# Revit family: Double_Check_Valve_Assembly-Backflow_Preventor-WATTS-LF909-909-AGK-NRS_Series.rfaxxx
name_source: partatom
category: Pipe Accessories
units: mm (PartAtom-declared; Revit-internal decimal feet)

## family parameters
Always vertical = Yes
Cut with Voids When Loaded = No
OmniClass Number = 23.65.55.14.21
OmniClass Title = Non-Return Valves for Liquid Services
Part Type = Valve - Breaks Into
Round Connector Dimension = Use Diameter
Shared = No
Work Plane-Based = No

## types (6) — shared parameters
909-AGF Air Gap = No
909-AGK Air Gap = Yes
909AG-K Dimension A = 6 3/8"
909AG-K Dimension B = 9 5/8"
909AG-K Dimension C = 3"
A.2 = 3 3/16"
ALERT- With SentryPlusTM Alert Flood Detection System = No
ASSE 1013 Certified = Yes
Assembly Code = F1050
C.2 = 1 1/2"
CW Connection = Yes
Country = United States of America
Description = LEAD FREE Series LF909-909-AGK-NRS Reduced Pressure Zone Backflow Assemblies Sizes: 2 1/2in to 10in
Finish- Check Valve Bodies Material = Cast Iron-Watts-Epoxy Coated
Finish- Seat = Metal-Watts-Stainless Steel
Finish- Trim = Metal-Watts-Stainless Steel
IAPMO Compliance = AWWA C511-92, IAPMO PS 31, SBCCI (Standard Plumbing Code), USC manual for Cross-Connection Control, 8th Edition
Installation Instruction Link = https://www.watts.com
LF- Without Shutoff Valves = No
Manufacturer = WATTS
Manufacturer Product Line = Reduced Pressure Zone Assemblies
Material = Cast Iron-Watts-Epoxy Coated
Max. Flow Rate = Typical Maximum Flow Rate (7.5 feet/sec.)
Max. Working Pressure = 175psi (12.06 bar)
NRS- Non-Rising Stem Resilient Seated Gate Valves = Yes
OSY- UL/FM Outside Stem & Yoke Resilient Seated Gate = No
Product Documentation Link = https://www.watts.com
Product Page URL = https://www.watts.com
QT-FDA- FDA Epoxy Coated Quarter-Turn Ball Valves = No
Region = North America
S-FDA - FDA Epoxy Coated Strainer = No
Temperature Range = 33°F-110°F (0.5°C-43°C) Continuous, 140°F (60°C) intermittent
URL = https://www.watts.com

## per-type parameters (varying)
- 2 1/2" LF909-909-AGK-NRS: (C) NRS=9 3/8"; -NRS H1 Dimension=7"; -NRS H1 Radius=3 1/2"; -NRS W Dimension=7 1/16"; -NRS W Radius=3 17/32"; A1 Dimension=20 3/4"; AG-K 2 Visibility 4"-10"=No; AG-K 2"-3"=Yes; D Dimension=5 1/4"; Diameter 1=3"; Diameter 2=1/4"; Diameter 3=2 1/2"; Distance 1=19/32"; Distance 2=29/32"; Flange Thickness=11/16"; Gap=2"; Height 1=7"; Height 2=27/32"; Height 3=1 13/32"; Inlet & Oulet Radius=1 1/4"; Inlet & Outlet Connection=2 1/2"; Inlet Description=2 1/2" OD Inlet Connection; L Dimension=26 5/16"; L_Radius=13 5/32"; NRS Weight=195 lbs (88.4 kg); Outlet Description=2 1/2" OD Outlet Connection; R Dimension=4"; T Dimension=9 1/16"; U Dimension=11"
- 10" LF909-909-AGK-NRS: (C) NRS=23 13/16"; -NRS H1 Dimension=16"; -NRS H1 Radius=8"; -NRS W Dimension=12 7/16"; -NRS W Radius=6 9/16"; A1 Dimension=46 3/4"; AG-K 2 Visibility 4"-10"=Yes; AG-K 2"-3"=No; D Dimension=9 3/4"; Diameter 1=8"; Diameter 2=1 1/32"; Diameter 3=6 1/4"; Distance 1=1 19/32"; Distance 2=2 13/32"; Flange Thickness=1 3/16"; Gap=2 1/32"; Height 1=20"; Height 2=3 11/32"; Height 3=4"; Inlet & Oulet Radius=5"; Inlet & Outlet Connection=10"; Inlet Description=10" OD Inlet Connection; L Dimension=67 5/16"; L_Radius=33 21/32"; NRS Weight=2160 lbs (980 kg); Outlet Description=10" OD Outlet Connection; R Dimension=12 1/2"; T Dimension=21"; U Dimension=21"
- 3" LF909-909-AGK-NRS: (C) NRS=10 1/4"; -NRS H1 Dimension=7 1/2"; -NRS H1 Radius=3 3/4"; -NRS W Dimension=7 7/8"; -NRS W Radius=3 15/16"; A1 Dimension=21 1/4"; AG-K 2 Visibility 4"-10"=No; AG-K 2"-3"=Yes; D Dimension=5 1/4"; Diameter 1=3 1/4"; Diameter 2=5/16"; Diameter 3=2 3/4"; Distance 1=21/32"; Distance 2=31/32"; Flange Thickness=3/4"; Gap=2"; Height 1=8"; Height 2=1"; Height 3=1 19/32"; Inlet & Oulet Radius=1 1/2"; Inlet & Outlet Connection=3"; Inlet Description=3" OD Inlet Connection; L Dimension=26 5/16"; L_Radius=13 5/32"; NRS Weight=225 lbs (102 kg); Outlet Description=3" OD Outlet Connection; R Dimension=5"; T Dimension=9 1/16"; U Dimension=11"
- 4" LF909-909-AGK-NRS: (C) NRS=12 3/16"; -NRS H1 Dimension=9"; -NRS H1 Radius=4 1/2"; -NRS W Dimension=10"; -NRS W Radius=4 17/32"; A1 Dimension=27 21/32"; AG-K 2 Visibility 4"-10"=Yes; AG-K 2"-3"=No; D Dimension=6"; Diameter 1=4 1/4"; Diameter 2=13/32"; Diameter 3=3 1/4"; Distance 1=27/32"; Distance 2=1 9/32"; Flange Thickness=15/16"; Gap=3 1/4"; Height 1=10"; Height 2=1 11/32"; Height 3=2"; Inlet & Oulet Radius=2"; Inlet & Outlet Connection=4"; Inlet Description=4" OD Inlet Connection; L Dimension=37 3/16"; L_Radius=18 19/32"; NRS Weight=455 lbs (206 kg); Outlet Description=4" OD Outlet Connection; R Dimension=6"; T Dimension=14 3/8"; U Dimension=14"
- 6" LF909-909-AGK-NRS: (C) NRS=16"; -NRS H1 Dimension=11"; -NRS H1 Radius=5 1/2"; -NRS W Dimension=11"; -NRS W Radius=5 11/32"; A1 Dimension=33"; AG-K 2 Visibility 4"-10"=Yes; AG-K 2"-3"=No; D Dimension=6"; Diameter 1=5 1/2"; Diameter 2=5/8"; Diameter 3=4 1/4"; Distance 1=1 3/32"; Distance 2=1 21/32"; Flange Thickness=1"; Gap=2 1/32"; Height 1=13"; Height 2=2"; Height 3=2 19/32"; Inlet & Oulet Radius=3"; Inlet & Outlet Connection=6"; Inlet Description=6" OD Inlet Connection; L Dimension=44 11/16"; L_Radius=22 11/32"; NRS Weight=718 lbs (326 kg); Outlet Description=6" OD Outlet Connection; R Dimension=11"; T Dimension=14 3/8"; U Dimension=16"
- 8" LF909-909-AGK-NRS: (C) NRS=19 15/16"; -NRS H1 Dimension=13 1/2"; -NRS H1 Radius=6 3/4"; -NRS W Dimension=11"; -NRS W Radius=5 27/32"; A1 Dimension=39 5/16"; AG-K 2 Visibility 4"-10"=Yes; AG-K 2"-3"=No; D Dimension=9 3/4"; Diameter 1=7"; Diameter 2=13/16"; Diameter 3=5 1/4"; Distance 1=1 13/32"; Distance 2=2 3/32"; Flange Thickness=1 1/8"; Gap=2 1/32"; Height 1=15"; Height 2=2 21/32"; Height 3=3"; Inlet & Oulet Radius=4"; Inlet & Outlet Connection=8"; Inlet Description=8" OD Inlet Connection; L Dimension=55 5/16"; L_Radius=27 21/32"; NRS Weight=1350 lbs (612 kg); Outlet Description=8" OD Outlet Connection; R Dimension=11 1/4"; T Dimension=19 1/4"; U Dimension=21"

note: column(s) folded — value = type name in every type: Model

## geometry (parser evidence)
native form markers: Sweep x4
no freeform markers — native parametric forms only
